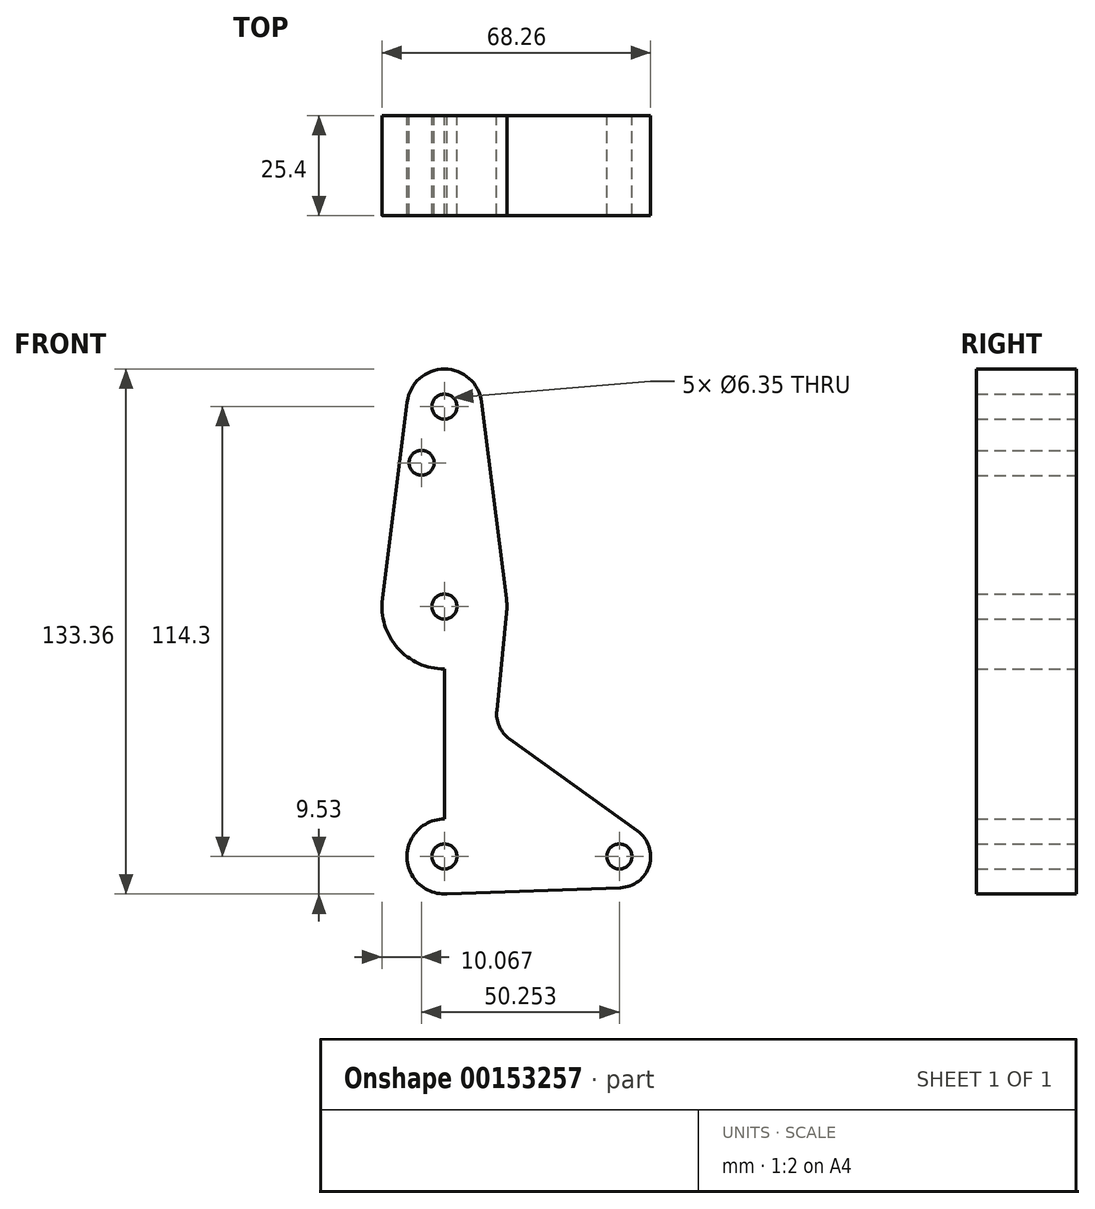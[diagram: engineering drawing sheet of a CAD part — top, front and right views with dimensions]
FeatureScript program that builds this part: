
annotation { "Feature Type Name" : "Feature", "Feature Type Description" : "" }
export const myFeature = defineFeature(function(context is Context, id is Id, definition is map)
    precondition{}
    {
        {
            var Q0;
            Q0=qCreatedBy(makeId("Front.planeOp"),FACE);
            var sketch = newSketch(context, id + "F0", { "sketchPlane" : qUnion([Q0])});
            skLineSegment(sketch, "E0", {"start": v(0, 0) * mm, "end": v(0, 63.5) * mm});
            skLineSegment(sketch, "E1", {"start": v(0, 63.5) * mm, "end": v(0, 114.3) * mm});
            skLineSegment(sketch, "E2", {"start": v(0, 0) * mm, "end": v(44.45, 0) * mm});
            skCircle(sketch, "E3", {"center": v(0, 0) * mm, "radius": 9.53 * mm});
            skCircle(sketch, "E4", {"center": v(44.45, 0) * mm, "radius": 7.94 * mm});
            skCircle(sketch, "E5", {"center": v(0, 63.5) * mm, "radius": 15.88 * mm});
            skCircle(sketch, "E6", {"center": v(0, 114.3) * mm, "radius": 9.53 * mm});
            skLineSegment(sketch, "E7", {"start": v(16.57, 29.84) * mm, "end": v(49.09, 6.44) * mm});
            skLineSegment(sketch, "E8", {"start": v(0, -9.53) * mm, "end": v(44.73, -7.93) * mm});
            skLineSegment(sketch, "E9", {"start": v(44.73, -7.93) * mm, "end": v(27.19, -8.56) * mm});
            skLineSegment(sketch, "E10", {"start": v(-9.45, 115.5) * mm, "end": v(-15.75, 65.48) * mm});
            skLineSegment(sketch, "E11", {"start": v(9.45, 115.5) * mm, "end": v(15.75, 65.48) * mm});
            skLineSegment(sketch, "E12", {"start": v(15.8, 61.91) * mm, "end": v(13.3, 37.1) * mm});
            skLineSegment(sketch, "E13", {"start": v(-15.8, 61.91) * mm, "end": v(-9.57, 0) * mm});
            skCircle(sketch, "E14", {"center": v(0, 114.3) * mm, "radius": 3.18 * mm});
            skCircle(sketch, "E15", {"center": v(0, 63.5) * mm, "radius": 3.18 * mm});
            skCircle(sketch, "E16", {"center": v(0, 0) * mm, "radius": 3.18 * mm});
            skCircle(sketch, "E17", {"center": v(44.45, 0) * mm, "radius": 3.18 * mm});
            skCircle(sketch, "E18", {"center": v(-5.8, 100.03) * mm, "radius": 3.18 * mm});
            skArc(sketch, "E19.filletArc", {"start": v(13.3, 37.1) * mm, "mid": v(13.96, 33.03) * mm, "end": v(16.57, 29.84) * mm});
            skPoint(sketch, "E20", {"position": v(91.41, 17.53) * mm});
            skSolve(sketch);
        }
        {
            var Q0;
            Q0 = qSketchRegion(id + "F0", true);
            extrude(context, id + "F1", {"entities" : qUnion([Q0]), "depth" : 25.4 * mm});
        }
    });
